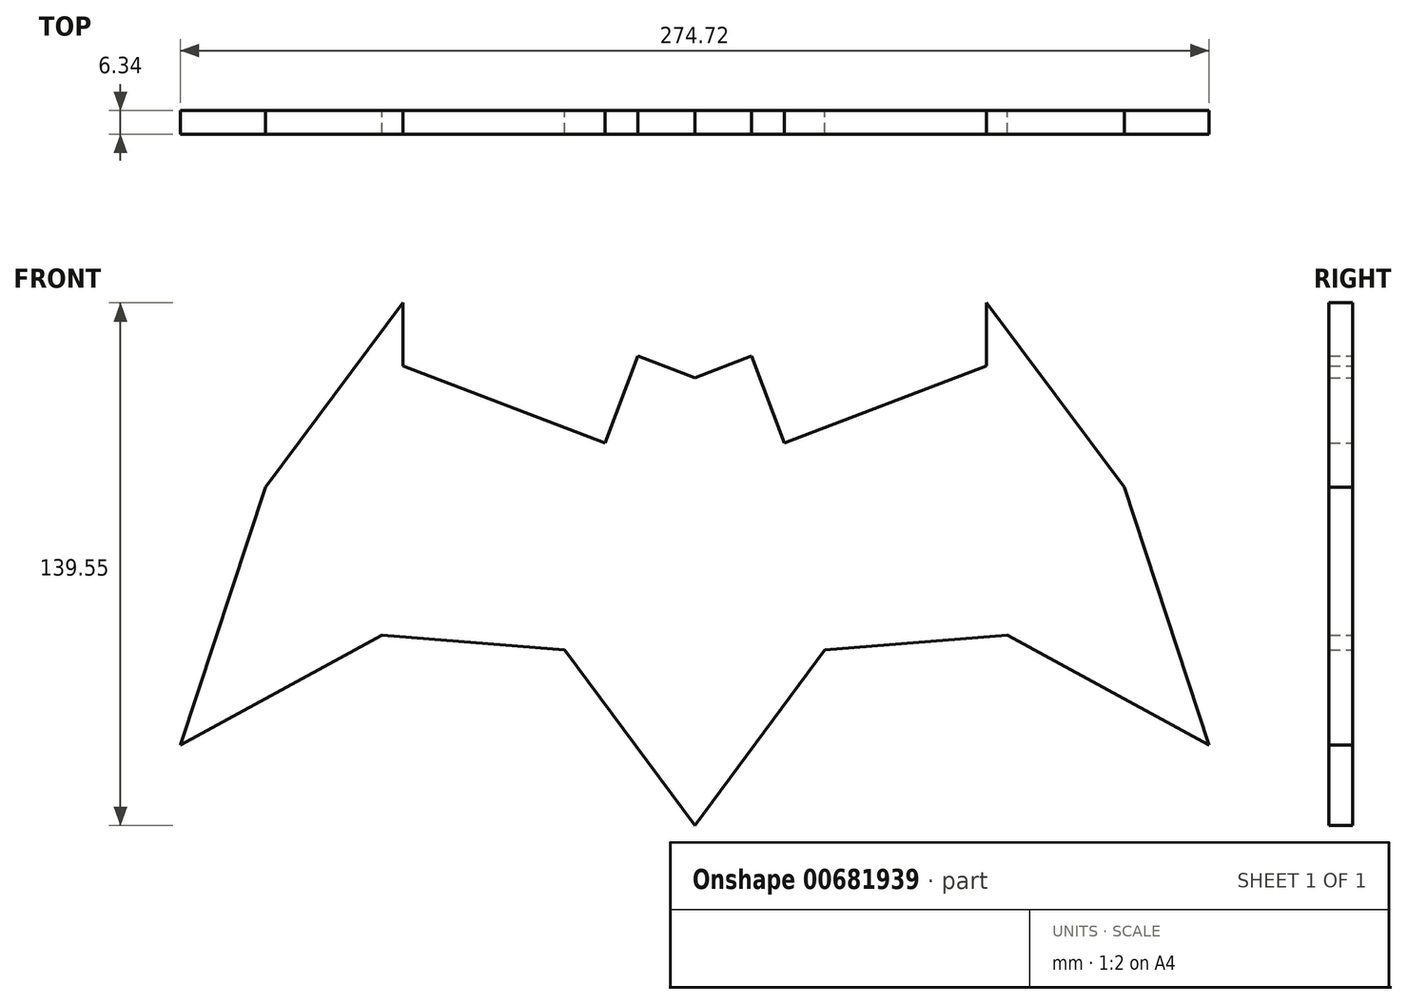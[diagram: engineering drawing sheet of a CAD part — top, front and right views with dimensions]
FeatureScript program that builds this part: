
annotation { "Feature Type Name" : "Feature", "Feature Type Description" : "" }
export const myFeature = defineFeature(function(context is Context, id is Id, definition is map)
    precondition{}
    {
        {
            var Q0;
            Q0=qCreatedBy(makeId("Front.planeOp"),FACE);
            var sketch = newSketch(context, id + "F0", { "sketchPlane" : qUnion([Q0])});
            skLineSegment(sketch, "E0", {"start": v(0, 37.79) * mm, "end": v(-15.12, 43.55) * mm});
            skLineSegment(sketch, "E1", {"start": v(-15.12, 43.55) * mm, "end": v(-23.96, 20.38) * mm});
            skLineSegment(sketch, "E2", {"start": v(-23.96, 20.38) * mm, "end": v(-77.93, 40.96) * mm});
            skLineSegment(sketch, "E3", {"start": v(-77.93, 40.96) * mm, "end": v(-77.93, 57.78) * mm});
            skLineSegment(sketch, "E4", {"start": v(-77.93, 57.78) * mm, "end": v(-114.68, 8.57) * mm});
            skLineSegment(sketch, "E5", {"start": v(-114.68, 8.57) * mm, "end": v(-137.36, -60.24) * mm});
            skLineSegment(sketch, "E6", {"start": v(-137.36, -60.24) * mm, "end": v(-83.55, -31.02) * mm});
            skLineSegment(sketch, "E7", {"start": v(-83.55, -31.02) * mm, "end": v(-34.73, -34.87) * mm});
            skLineSegment(sketch, "E8", {"start": v(-34.73, -34.87) * mm, "end": v(0, -81.77) * mm});
            skLineSegment(sketch, "E9", {"start": v(0, -81.77) * mm, "end": v(0, 37.79) * mm});
            skLineSegment(sketch, "E10.MirrorCS", {"start": v(0, 37.79) * mm, "end": v(15.12, 43.55) * mm});
            skLineSegment(sketch, "E11.MirrorCS", {"start": v(15.12, 43.55) * mm, "end": v(23.96, 20.38) * mm});
            skLineSegment(sketch, "E12.MirrorCS", {"start": v(23.96, 20.38) * mm, "end": v(77.93, 40.96) * mm});
            skLineSegment(sketch, "E13.MirrorCS", {"start": v(77.93, 40.96) * mm, "end": v(77.93, 57.78) * mm});
            skLineSegment(sketch, "E14.MirrorCS", {"start": v(77.93, 57.78) * mm, "end": v(114.68, 8.57) * mm});
            skLineSegment(sketch, "E15.MirrorCS", {"start": v(114.68, 8.57) * mm, "end": v(137.36, -60.24) * mm});
            skLineSegment(sketch, "E16.MirrorCS", {"start": v(137.36, -60.24) * mm, "end": v(83.55, -31.02) * mm});
            skLineSegment(sketch, "E17.MirrorCS", {"start": v(83.55, -31.02) * mm, "end": v(34.73, -34.87) * mm});
            skLineSegment(sketch, "E18.MirrorCS", {"start": v(34.73, -34.87) * mm, "end": v(0, -81.77) * mm});
            skSolve(sketch);
        }
        {
            var Q0;
            Q0=makeQuery(id+"F0.imprint","IMPRINT",FACE,{"disambiguationData":[TD([[makeQuery(id+"F0.imprint","IMPRINT",EDGE,{"derivedFrom":sQuery(id+"F0.wireOp",EDGE,"E0")}),1.0]])]});
            var Q1;
            Q1=makeQuery(id+"F0.imprint","IMPRINT",FACE,{"disambiguationData":[TD([[makeQuery(id+"F0.imprint","IMPRINT",EDGE,{"derivedFrom":sQuery(id+"F0.wireOp",EDGE,"E9")}),-1.0]])]});
            extrude(context, id + "F1", {"entities" : qUnion([Q0, Q1]), "endBound" : BoundingType.SYMMETRIC, "depth" : 6.35 * mm, "offsetDistance" : 25.4 * mm});
        }
    });
